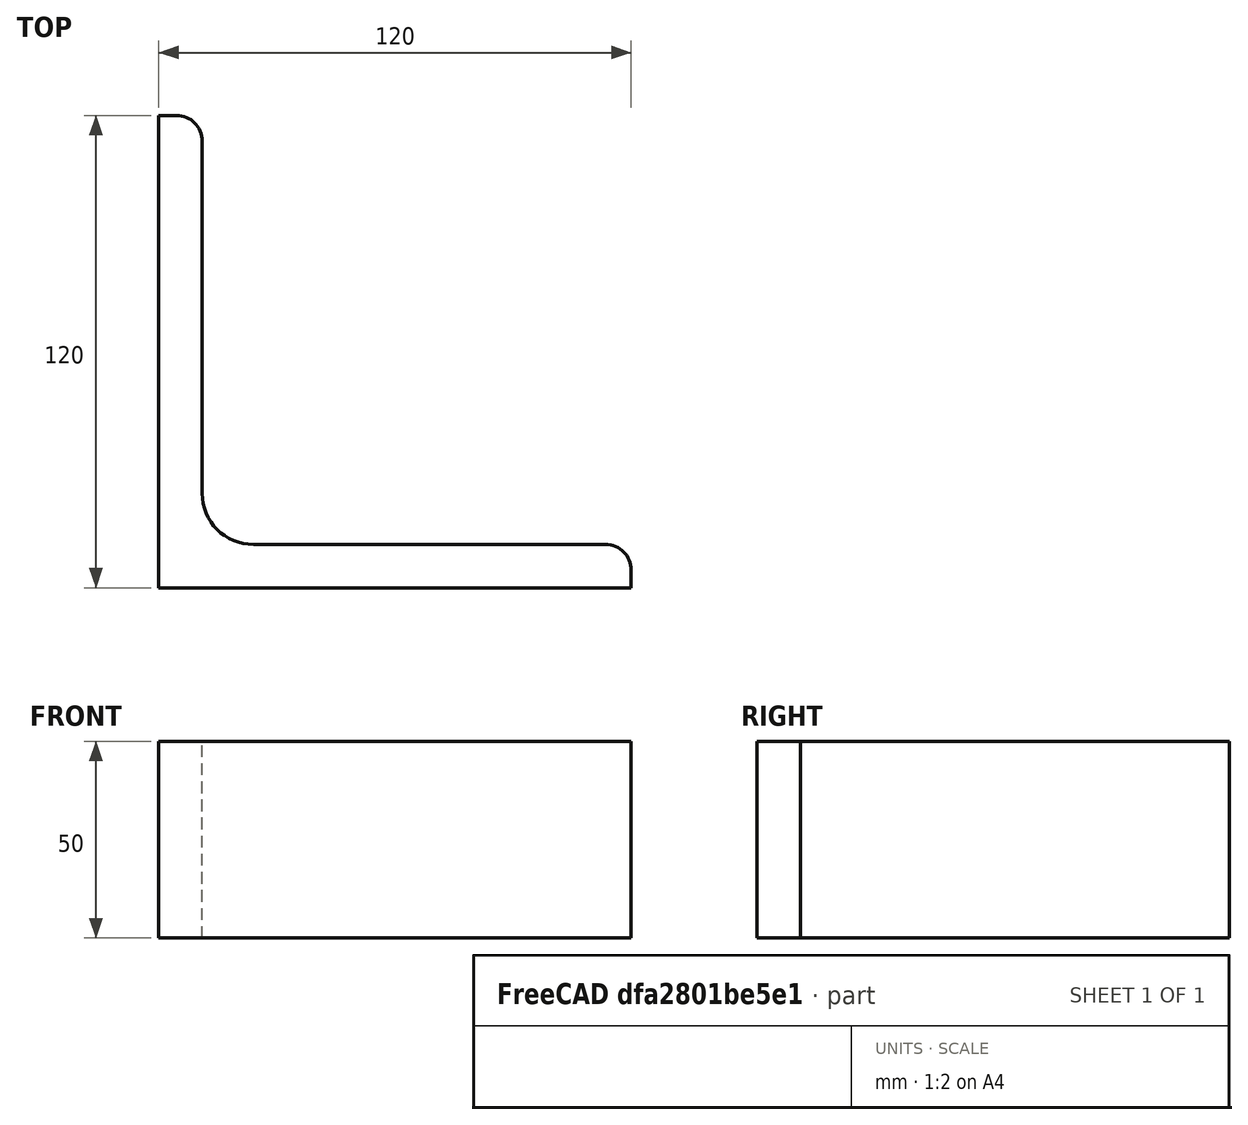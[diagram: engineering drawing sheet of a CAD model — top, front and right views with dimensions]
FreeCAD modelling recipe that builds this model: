
FCSTD DOCUMENT  (FreeCAD 0.15R4671 (Git))
Label: Angle Bar L120x120x11 EN10056 S235JR
License: All rights reserved
LicenseURL: http://en.wikipedia.org/wiki/All_rights_reserved
objects: Sketcher::SketchObject×1, Part::Extrusion×1
note: 2 computed .brp shape members not serialized (recipe doc carries the construction recipe); baked Part::Feature solids carry a one-line shape summary decoded from their .brp

FEATURE [Sketcher::SketchObject] Sketch
  sketch-geometry (9):
    g0: LineSegment StartX=0 StartY=0 StartZ=0 EndX=120 EndY=0 EndZ=0
    g1: LineSegment StartX=120 StartY=0 StartZ=0 EndX=120 EndY=4.5 EndZ=0
    g2: LineSegment StartX=113.5 StartY=11 StartZ=0 EndX=24 EndY=11 EndZ=0
    g3: LineSegment StartX=0 StartY=0 StartZ=0 EndX=0 EndY=120 EndZ=0
    g4: LineSegment StartX=0 StartY=120 StartZ=0 EndX=4.5 EndY=120 EndZ=0
    g5: LineSegment StartX=11 StartY=113.5 StartZ=0 EndX=11 EndY=24 EndZ=0
    g6: ArcOfCircle CenterX=24 CenterY=24 CenterZ=0 NormalX=0 NormalY=0 NormalZ=1 Radius=13 StartAngle=3.14159 EndAngle=4.71239
    g7: ArcOfCircle CenterX=4.5 CenterY=113.5 CenterZ=0 NormalX=0 NormalY=0 NormalZ=1 Radius=6.5 StartAngle=0 EndAngle=1.5708
    g8: ArcOfCircle CenterX=113.5 CenterY=4.5 CenterZ=0 NormalX=0 NormalY=0 NormalZ=1 Radius=6.5 StartAngle=0 EndAngle=1.5708
  constraints (23):
    c: Coincident(g0,g-1)
    c: Horizontal(g0)
    c: Coincident(g1,g0)
    c: Vertical(g1)
    c: Horizontal(g2)
    c: Coincident(g3,g-1)
    c: Vertical(g3)
    c: Coincident(g4,g3)
    c: Horizontal(g4)
    c: Vertical(g5)
    c: Tangent(g5,g6) = -1.5708
    c: Tangent(g2,g6) = 1.5708
    c: Tangent(g4,g7) = 1.5708
    c: Tangent(g5,g7) = 1.5708
    c: Tangent(g2,g8) = -1.5708
    c: Tangent(g1,g8) = -1.5708
    c: DistanceX(g0) = 120
    c: DistanceY(g3) = 120
    c: DistanceY(g0,g2) = 11
    c: DistanceX(g3,g5) = 11
    c: Radius(g6) = 13
    c: Radius(g8) = 6.5
    c: Radius(g7) = 6.5
FEATURE [Part::Extrusion] Extrude  label="Angle Bar L120x120x11 EN10056 S235JR"
  Base = -> Sketch
  Dir = (0,0,50)
  Solid = true
